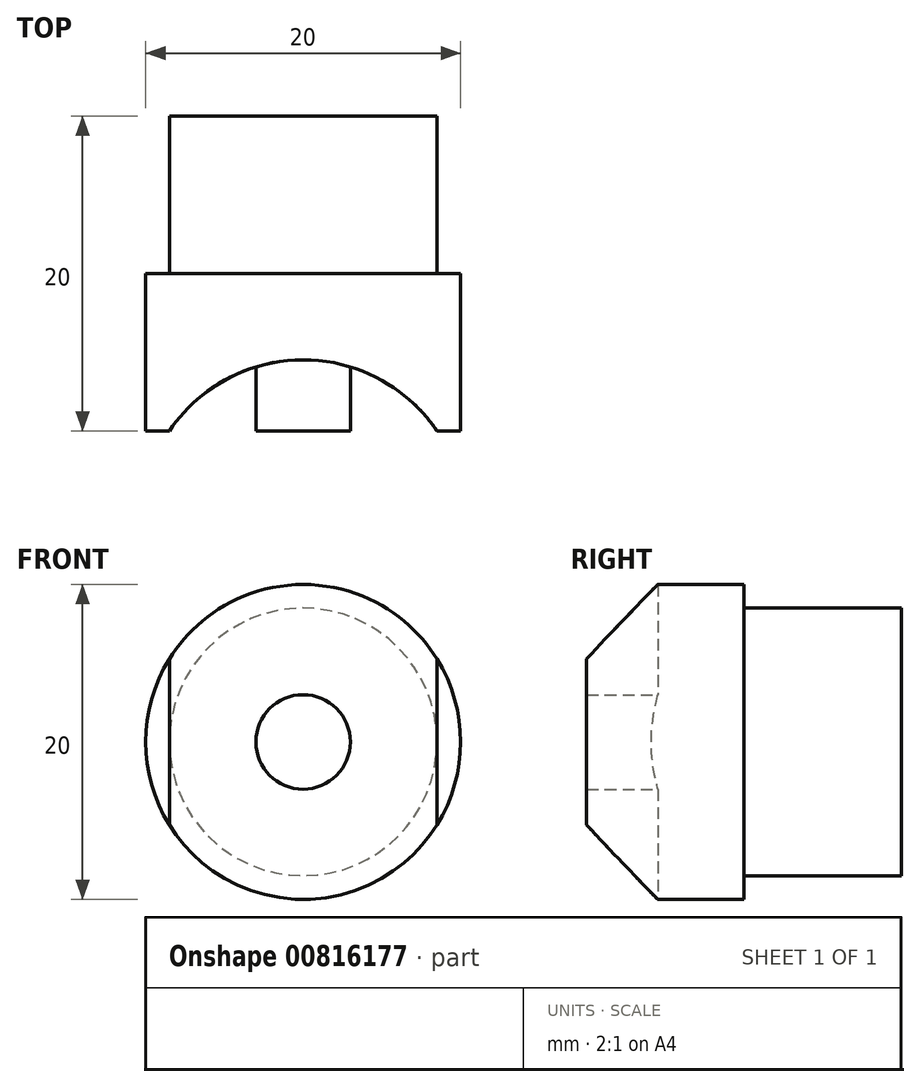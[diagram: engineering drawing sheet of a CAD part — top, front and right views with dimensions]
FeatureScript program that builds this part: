
annotation { "Feature Type Name" : "Feature", "Feature Type Description" : "" }
export const myFeature = defineFeature(function(context is Context, id is Id, definition is map)
    precondition{}
    {
        {
            var Q0;
            Q0=qCreatedBy(makeId("Top.planeOp"),FACE);
            var sketch = newSketch(context, id + "F0", { "sketchPlane" : qUnion([Q0])});
            skLineSegment(sketch, "E0.bottom", {"start": v(-18.5, 20) * mm, "end": v(-1.5, 20) * mm});
            skLineSegment(sketch, "E0.top", {"start": v(-18.5, 0) * mm, "end": v(-1.5, 0) * mm});
            skLineSegment(sketch, "E0.left", {"start": v(-18.5, 20) * mm, "end": v(-18.5, 0) * mm});
            skLineSegment(sketch, "E0.right", {"start": v(-1.5, 20) * mm, "end": v(-1.5, 0) * mm});
            skLineSegment(sketch, "E1.bottom", {"start": v(0, 0) * mm, "end": v(-20, 0) * mm});
            skLineSegment(sketch, "E1.top", {"start": v(0, 10) * mm, "end": v(-20, 10) * mm});
            skLineSegment(sketch, "E1.left", {"start": v(0, 0) * mm, "end": v(0, 10) * mm});
            skLineSegment(sketch, "E1.right", {"start": v(-20, 0) * mm, "end": v(-20, 10) * mm});
            skCircle(sketch, "E2", {"center": v(-10, -5.73) * mm, "radius": 10.25 * mm});
            skPoint(sketch, "E2.centerSnap0", {"position": v(-10, 0) * mm});
            skLineSegment(sketch, "E3.bottom", {"start": v(-13, 4.52) * mm, "end": v(-7, 4.52) * mm});
            skLineSegment(sketch, "E3.top", {"start": v(-13, 0) * mm, "end": v(-7, 0) * mm});
            skLineSegment(sketch, "E3.left", {"start": v(-13, 4.52) * mm, "end": v(-13, 0) * mm});
            skLineSegment(sketch, "E3.right", {"start": v(-7, 4.52) * mm, "end": v(-7, 0) * mm});
            skLineSegment(sketch, "E4", {"start": v(-10, 20) * mm, "end": v(-10, 0) * mm});
            skSolve(sketch);
        }
        {
            var Q0;
            {var subQ0=sQuery(id+"F0.wireOp",EDGE,"E4");var subQ9=sQuery(id+"F0.wireOp",EDGE,"E1.top");var subQ10=makeQuery(id+"F0.imprint","INTERSECT",VERTEX,{"derivedFrom":[subQ9,subQ0]});Q0=makeQuery(id+"F0.imprint","IMPRINT",FACE,{"disambiguationData":[TD([[makeQuery(id+"F0.imprint","IMPRINT",EDGE,{"disambiguationData":[TD([[subQ10,-1.0]])],"derivedFrom":subQ9}),1.0]])]});}
            var Q1;
            {var subQ5=sQuery(id+"F0.wireOp",EDGE,"E1.right");Q1=makeQuery(id+"F0.imprint","IMPRINT",FACE,{"disambiguationData":[TD([[makeQuery(id+"F0.imprint","IMPRINT",EDGE,{"derivedFrom":subQ5}),-1.0]])]});}
            var Q2;
            {var subQ0=sQuery(id+"F0.wireOp",EDGE,"E0.left");var subQ1=sQuery(id+"F0.wireOp",EDGE,"E0.bottom");var subQ2=makeQuery(id+"F0.imprint","INTERSECT",VERTEX,{"derivedFrom":[subQ1,subQ0]});Q2=makeQuery(id+"F0.imprint","IMPRINT",FACE,{"disambiguationData":[TD([[makeQuery(id+"F0.imprint","IMPRINT",EDGE,{"disambiguationData":[TD([[subQ2,-1.0]])],"derivedFrom":subQ1}),-1.0]])]});}
            var Q3;
            {var subQ1=sQuery(id+"F0.wireOp",EDGE,"E2");var subQ3=sQuery(id+"F0.wireOp",EDGE,"E3.left");var subQ4=makeQuery(id+"F0.imprint","INTERSECT",VERTEX,{"derivedFrom":[subQ1,subQ3]});Q3=makeQuery(id+"F0.imprint","IMPRINT",FACE,{"disambiguationData":[TD([[makeQuery(id+"F0.imprint","IMPRINT",EDGE,{"disambiguationData":[TD([[subQ4,1.0]])],"derivedFrom":subQ3}),1.0]])]});}
            var Q4;
            {var subQ0=sQuery(id+"F0.wireOp",EDGE,"E4");var subQ1=sQuery(id+"F0.wireOp",EDGE,"E0.top");var subQ2=makeQuery(id+"F0.imprint","INTERSECT",VERTEX,{"derivedFrom":[subQ1,subQ0]});Q4=makeQuery(id+"F0.imprint","IMPRINT",FACE,{"disambiguationData":[TD([[makeQuery(id+"F0.imprint","IMPRINT",EDGE,{"disambiguationData":[TD([[subQ2,1.0]])],"derivedFrom":subQ1}),1.0]])]});}
            var Q5;
            {var subQ0=sQuery(id+"F0.wireOp",EDGE,"E2");var subQ3=sQuery(id+"F0.wireOp",EDGE,"E3.left");var subQ5=makeQuery(id+"F0.imprint","INTERSECT",VERTEX,{"derivedFrom":[subQ0,subQ3]});Q5=makeQuery(id+"F0.imprint","IMPRINT",FACE,{"disambiguationData":[TD([[makeQuery(id+"F0.imprint","IMPRINT",EDGE,{"disambiguationData":[TD([[subQ5,-1.0]])],"derivedFrom":subQ3}),-1.0]])]});}
            var Q6;
            Q6=sQuery(id+"F0.wireOp",EDGE,"E4");
            revolve(context, id + "F1", {"surfaceOperationType" : NewSurfaceOperationType.NEW, "entities" : qUnion([Q0, Q1, Q2, Q3, Q4, Q5]), "axis" : qUnion([Q6]), "revolveType" : RevolveType.FULL});
        }
        {
            var Q0;
            {var subQ0=sQuery(id+"F0.wireOp",EDGE,"E2");var subQ3=sQuery(id+"F0.wireOp",EDGE,"E3.left");var subQ5=makeQuery(id+"F0.imprint","INTERSECT",VERTEX,{"derivedFrom":[subQ0,subQ3]});Q0=makeQuery(id+"F0.imprint","IMPRINT",FACE,{"disambiguationData":[TD([[makeQuery(id+"F0.imprint","IMPRINT",EDGE,{"disambiguationData":[TD([[subQ5,-1.0]])],"derivedFrom":subQ3}),-1.0]])]});}
            var Q1;
            {var subQ0=sQuery(id+"F0.wireOp",EDGE,"E3.right");var subQ1=sQuery(id+"F0.wireOp",EDGE,"E0.top");var subQ2=makeQuery(id+"F0.imprint","INTERSECT",VERTEX,{"derivedFrom":[subQ1,subQ0]});Q1=makeQuery(id+"F0.imprint","IMPRINT",FACE,{"disambiguationData":[TD([[makeQuery(id+"F0.imprint","IMPRINT",EDGE,{"disambiguationData":[TD([[subQ2,1.0]])],"derivedFrom":subQ0}),1.0]])]});}
            var Q2;
            {var subQ0=sQuery(id+"F0.wireOp",EDGE,"E4");var subQ1=sQuery(id+"F0.wireOp",EDGE,"E0.top");var subQ2=makeQuery(id+"F0.imprint","INTERSECT",VERTEX,{"derivedFrom":[subQ1,subQ0]});Q2=makeQuery(id+"F0.imprint","IMPRINT",FACE,{"disambiguationData":[TD([[makeQuery(id+"F0.imprint","IMPRINT",EDGE,{"disambiguationData":[TD([[subQ2,1.0]])],"derivedFrom":subQ1}),1.0]])]});}
            var Q3;
            {var subQ0=sQuery(id+"F0.wireOp",EDGE,"E3.right");var subQ1=sQuery(id+"F0.wireOp",EDGE,"E0.top");var subQ2=makeQuery(id+"F0.imprint","INTERSECT",VERTEX,{"derivedFrom":[subQ1,subQ0]});Q3=makeQuery(id+"F0.imprint","IMPRINT",FACE,{"disambiguationData":[TD([[makeQuery(id+"F0.imprint","IMPRINT",EDGE,{"disambiguationData":[TD([[subQ2,1.0]])],"derivedFrom":subQ1}),1.0]])]});}
            extrude(context, id + "F2", {"entities" : qUnion([Q0, Q1, Q2, Q3]), "operationType" : NewBodyOperationType.REMOVE, "depth" : 25 * mm, "offsetDistance" : 25 * mm, "hasSecondDirection" : true, "secondDirectionOppositeDirection" : true, "secondDirectionDepth" : 25 * mm});
        }
        {
            var Q0;
            {var subQ0=sQuery(id+"F0.wireOp",EDGE,"E4");var subQ1=sQuery(id+"F0.wireOp",EDGE,"E0.top");var subQ2=makeQuery(id+"F0.imprint","INTERSECT",VERTEX,{"derivedFrom":[subQ1,subQ0]});Q0=makeQuery(id+"F0.imprint","IMPRINT",FACE,{"disambiguationData":[TD([[makeQuery(id+"F0.imprint","IMPRINT",EDGE,{"disambiguationData":[TD([[subQ2,1.0]])],"derivedFrom":subQ1}),1.0]])]});}
            var Q1;
            {var subQ1=sQuery(id+"F0.wireOp",EDGE,"E2");var subQ3=sQuery(id+"F0.wireOp",EDGE,"E3.left");var subQ4=makeQuery(id+"F0.imprint","INTERSECT",VERTEX,{"derivedFrom":[subQ1,subQ3]});Q1=makeQuery(id+"F0.imprint","IMPRINT",FACE,{"disambiguationData":[TD([[makeQuery(id+"F0.imprint","IMPRINT",EDGE,{"disambiguationData":[TD([[subQ4,1.0]])],"derivedFrom":subQ3}),1.0]])]});}
            var Q2;
            Q2=sQuery(id+"F0.wireOp",EDGE,"E4");
            revolve(context, id + "F3", {"operationType" : NewBodyOperationType.ADD, "surfaceOperationType" : NewSurfaceOperationType.NEW, "entities" : qUnion([Q0, Q1]), "axis" : qUnion([Q2]), "revolveType" : RevolveType.FULL});
        }
    });
